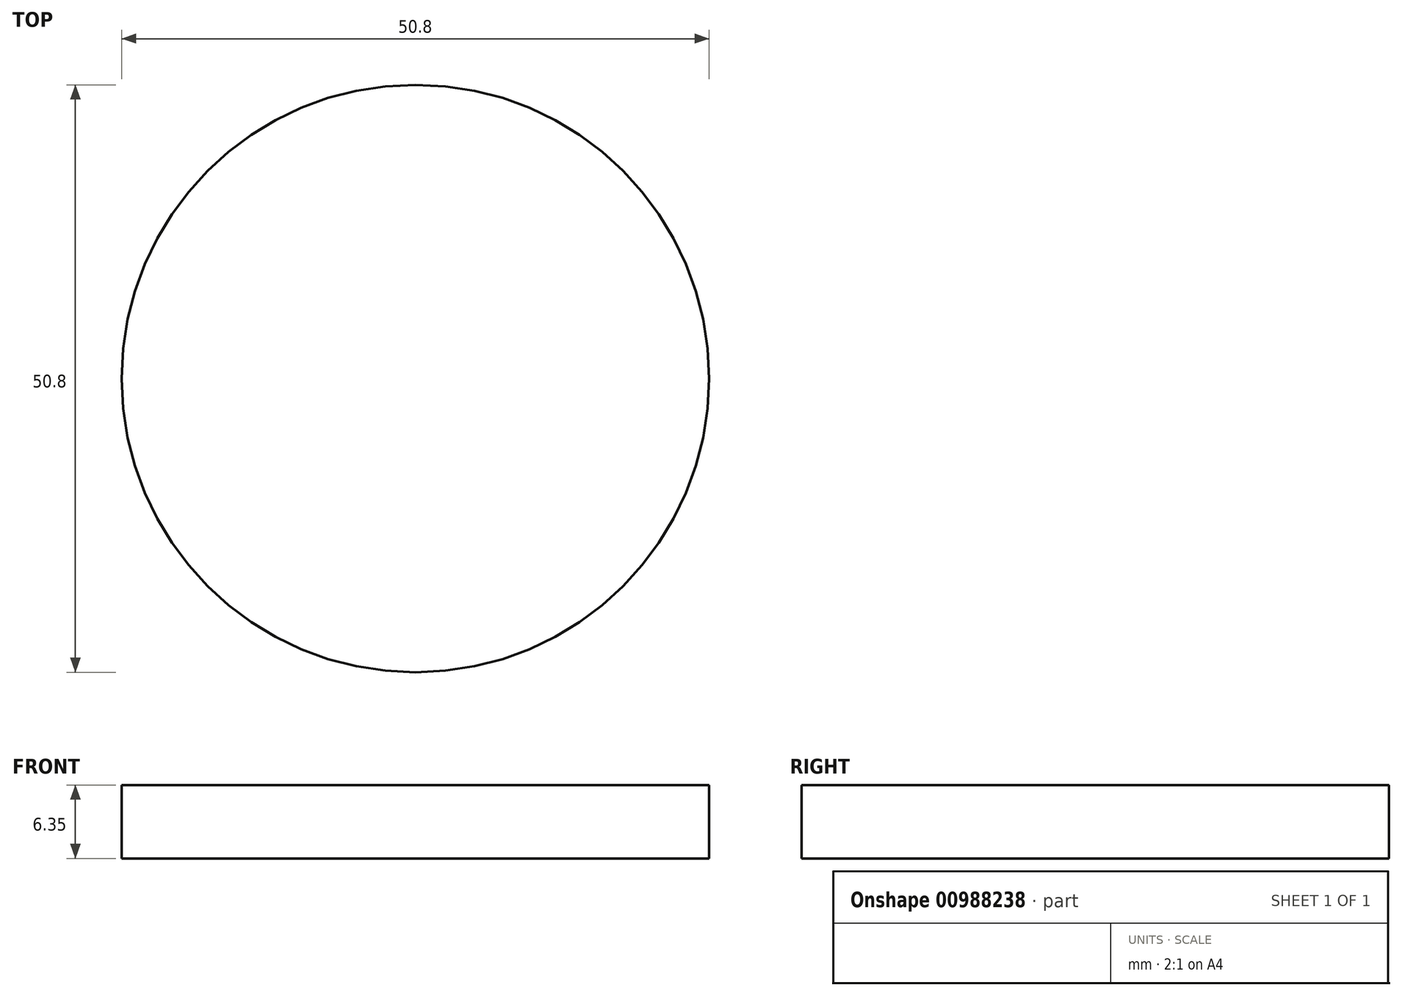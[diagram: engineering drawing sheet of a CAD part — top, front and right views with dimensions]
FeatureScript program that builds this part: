
annotation { "Feature Type Name" : "Feature", "Feature Type Description" : "" }
export const myFeature = defineFeature(function(context is Context, id is Id, definition is map)
    precondition{}
    {
        {
            var Q0;
            Q0=qCreatedBy(makeId("Top.planeOp"),FACE);
            var sketch = newSketch(context, id + "F0", { "sketchPlane" : qUnion([Q0])});
            skCircle(sketch, "E0", {"center": v(0, 0) * mm, "radius": 25.4 * mm});
            skSolve(sketch);
        }
        {
            var Q0;
            Q0 = qSketchRegion(id + "F0", true);
            extrude(context, id + "F1", {"entities" : qUnion([Q0]), "depth" : 6.35 * mm, "offsetDistance" : 25.4 * mm});
        }
    });
